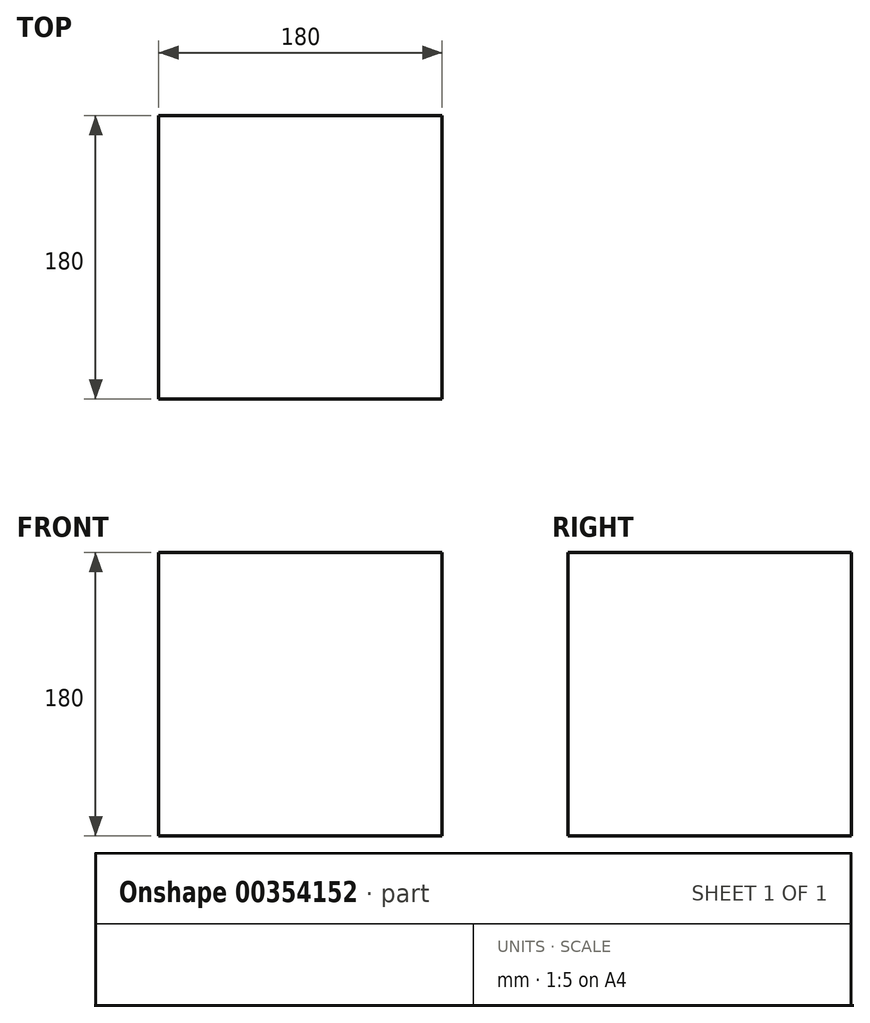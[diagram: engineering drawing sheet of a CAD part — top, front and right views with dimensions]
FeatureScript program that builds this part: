
annotation { "Feature Type Name" : "Feature", "Feature Type Description" : "" }
export const myFeature = defineFeature(function(context is Context, id is Id, definition is map)
    precondition{}
    {
        {
            var Q0;
            Q0=qCreatedBy(makeId("Front.planeOp"),FACE);
            var sketch = newSketch(context, id + "F0", { "sketchPlane" : qUnion([Q0])});
            skLineSegment(sketch, "E0.bottom", {"start": v(-93.64, 101.4) * mm, "end": v(86.36, 101.4) * mm});
            skLineSegment(sketch, "E0.top", {"start": v(-93.64, -78.6) * mm, "end": v(86.36, -78.6) * mm});
            skLineSegment(sketch, "E0.left", {"start": v(-93.64, 101.4) * mm, "end": v(-93.64, -78.6) * mm});
            skLineSegment(sketch, "E0.right", {"start": v(86.36, 101.4) * mm, "end": v(86.36, -78.6) * mm});
            skSolve(sketch);
        }
        {
            var Q0;
            Q0 = qSketchRegion(id + "F0", true);
            extrude(context, id + "F1", {"entities" : qUnion([Q0]), "depth" : 180 * mm});
        }
    });
